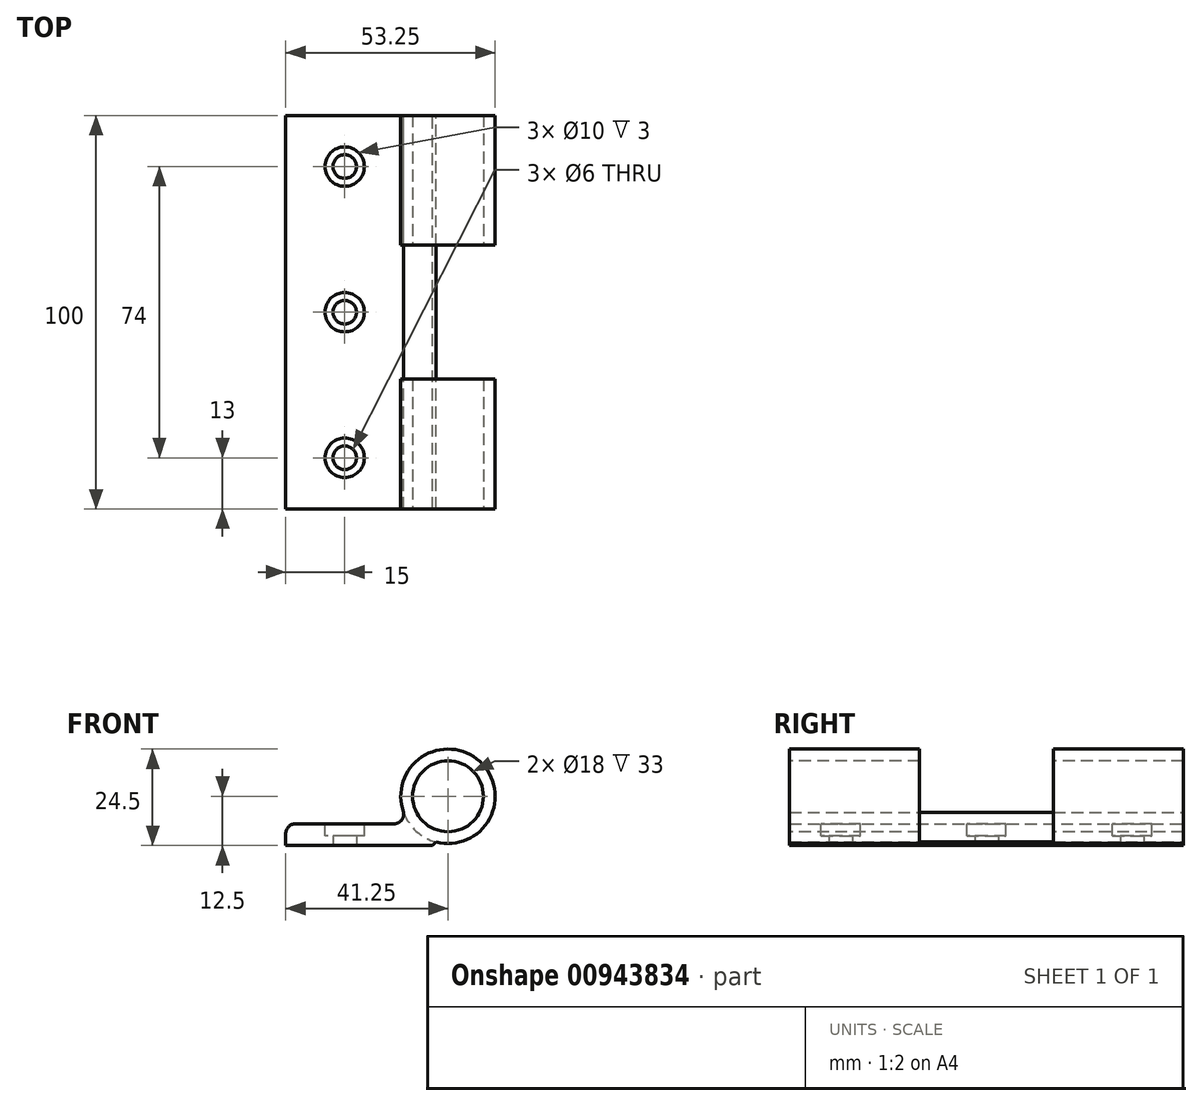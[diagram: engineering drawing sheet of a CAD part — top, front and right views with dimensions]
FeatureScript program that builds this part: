
annotation { "Feature Type Name" : "Feature", "Feature Type Description" : "" }
export const myFeature = defineFeature(function(context is Context, id is Id, definition is map)
    precondition{}
    {
        {
            var Q0;
            Q0=qCreatedBy(makeId("Front.planeOp"),FACE);
            var sketch = newSketch(context, id + "F0", { "sketchPlane" : qUnion([Q0])});
            skLineSegment(sketch, "E0.top", {"start": v(0, 5.5) * mm, "end": v(27.5, 5.5) * mm});
            skLineSegment(sketch, "E0.left", {"start": v(0, 0) * mm, "end": v(0, 5.5) * mm});
            skLineSegment(sketch, "E1", {"start": v(41.25, 12.5) * mm, "end": v(41.25, 0) * mm, "construction": true});
            skCircle(sketch, "E2", {"center": v(41.25, 12.5) * mm, "radius": 12 * mm});
            skLineSegment(sketch, "E3", {"start": v(41.25, 12.5) * mm, "end": v(0, 12.5) * mm, "construction": true});
            skArc(sketch, "E4", {"start": v(27.5, 5.5) * mm, "mid": v(29.41, 6.39) * mm, "end": v(29.96, 8.42) * mm});
            skLineSegment(sketch, "E5", {"start": v(37.37, 0) * mm, "end": v(38.25, 0.88) * mm});
            skLineSegment(sketch, "E6", {"start": v(0, 0) * mm, "end": v(37.37, 0) * mm});
            skSolve(sketch);
        }
        {
            var Q0;
            Q0 = qSketchRegion(id + "F0", true);
            extrude(context, id + "F1", {"entities" : qUnion([Q0]), "depth" : 100 * mm, "offsetDistance" : 25 * mm, "symmetric" : true});
        }
        {
            var Q0;
            Q0=makeQuery(id+"F1.opExtrude","SWEPT_EDGE",EDGE,{"disambiguationData":[OSD([sQuery(id+"F0.wireOp",EDGE,"E0.top"),sQuery(id+"F0.wireOp",EDGE,"E0.left")])]});
            fillet(context, id + "F2", {"entities" : qUnion([Q0]), "radius" : 2.5 * mm, "tangentPropagation" : true, "allowEdgeOverflow" : false});
        }
        {
            var Q0;
            Q0=makeQuery(id+"F1.opExtrude","CAP_FACE",FACE,{"disambiguationData":[OSD([sQuery(id+"F0.wireOp",EDGE,"E0.top"),sQuery(id+"F0.wireOp",EDGE,"E0.left"),sQuery(id+"F0.wireOp",EDGE,"E2"),sQuery(id+"F0.wireOp",EDGE,"E4"),sQuery(id+"F0.wireOp",EDGE,"E5"),sQuery(id+"F0.wireOp",EDGE,"E6")])],"isStart":false});
            var sketch = newSketch(context, id + "F3", { "sketchPlane" : qUnion([Q0])});
            skCircle(sketch, "E7", {"center": v(41.25, 12.5) * mm, "radius": 9 * mm});
            skSolve(sketch);
        }
        {
            var Q0;
            Q0 = qSketchRegion(id + "F3", true);
            extrude(context, id + "F4", {"entities" : qUnion([Q0]), "operationType" : NewBodyOperationType.REMOVE, "endBound" : BoundingType.UP_TO_NEXT, "oppositeDirection" : true, "depth" : 25 * mm, "offsetDistance" : 25 * mm});
        }
        {
            var Q0;
            Q0=makeQuery(id+"F1.opExtrude","CAP_FACE",FACE,{"disambiguationData":[OSD([sQuery(id+"F0.wireOp",EDGE,"E0.top"),sQuery(id+"F0.wireOp",EDGE,"E0.left"),sQuery(id+"F0.wireOp",EDGE,"E2"),sQuery(id+"F0.wireOp",EDGE,"E4"),sQuery(id+"F0.wireOp",EDGE,"E5"),sQuery(id+"F0.wireOp",EDGE,"E6")])],"isStart":false});
            var sketch = newSketch(context, id + "F5", { "sketchPlane" : qUnion([Q0])});
            skCircle(sketch, "E8", {"center": v(41.25, 12.5) * mm, "radius": 12 * mm});
            skSolve(sketch);
        }
        {
            var Q0;
            Q0 = qSketchRegion(id + "F5", true);
            extrude(context, id + "F6", {"entities" : qUnion([Q0]), "operationType" : NewBodyOperationType.REMOVE, "oppositeDirection" : true, "depth" : 67 * mm, "offsetDistance" : 25 * mm, "hasSecondDirection" : true, "secondDirectionOppositeDirection" : true, "secondDirectionDepth" : 33 * mm});
        }
        {
            var Q0;
            Q0=makeQuery(id+"F1.opExtrude","SWEPT_FACE",FACE,{"disambiguationData":[OSD([sQuery(id+"F0.wireOp",EDGE,"E0.top")])]});
            var sketch = newSketch(context, id + "F7", { "sketchPlane" : qUnion([Q0])});
            skCircle(sketch, "E9", {"center": v(15, 0) * mm, "radius": 5 * mm});
            skLineSegment(sketch, "E10", {"start": v(15, 50) * mm, "end": v(15, -50) * mm, "construction": true});
            skCircle(sketch, "E11", {"center": v(15, 37) * mm, "radius": 5 * mm});
            skCircle(sketch, "E12", {"center": v(15, -37) * mm, "radius": 5 * mm});
            skSolve(sketch);
        }
        {
            var Q0;
            Q0=makeQuery(id+"F1.opExtrude","SWEPT_FACE",FACE,{"disambiguationData":[OSD([sQuery(id+"F0.wireOp",EDGE,"E6")])]});
            var sketch = newSketch(context, id + "F8", { "sketchPlane" : qUnion([Q0])});
            skCircle(sketch, "E13", {"center": v(15, -37) * mm, "radius": 3 * mm});
            skCircle(sketch, "E14", {"center": v(15, 0) * mm, "radius": 3 * mm});
            skCircle(sketch, "E15", {"center": v(15, 37) * mm, "radius": 3 * mm});
            skSolve(sketch);
        }
        {
            var Q0;
            Q0 = qSketchRegion(id + "F7", true);
            extrude(context, id + "F9", {"entities" : qUnion([Q0]), "operationType" : NewBodyOperationType.REMOVE, "oppositeDirection" : true, "depth" : 3 * mm, "offsetDistance" : 25 * mm});
        }
        {
            var Q0;
            Q0 = qSketchRegion(id + "F8", true);
            extrude(context, id + "F10", {"entities" : qUnion([Q0]), "operationType" : NewBodyOperationType.REMOVE, "endBound" : BoundingType.UP_TO_NEXT, "oppositeDirection" : true, "depth" : 25 * mm, "offsetDistance" : 25 * mm});
        }
    });
